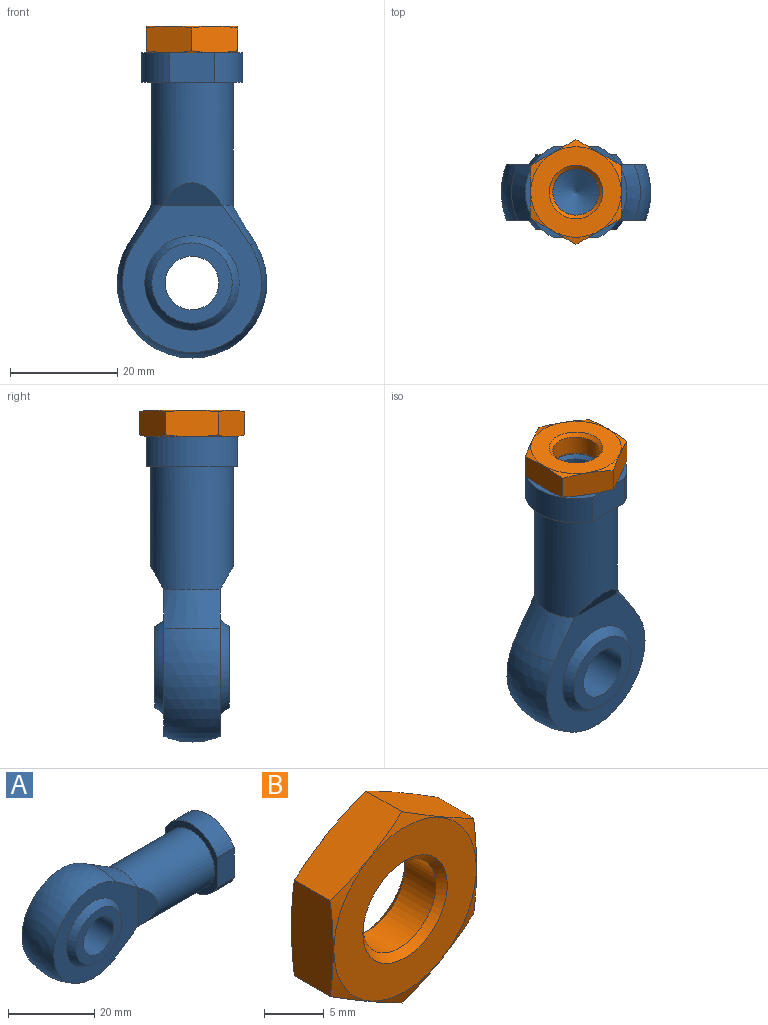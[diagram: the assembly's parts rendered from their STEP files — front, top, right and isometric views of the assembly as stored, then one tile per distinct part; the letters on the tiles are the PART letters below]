
ASSEMBLY  parts=2 mates=1
PART A: 22 faces, bbox 57x28x28 mm
  f0: cone r=866.03mm half-angle=60deg, axis (1,0,0), area 67.8mm2, adj f1
  f1: cylinder r=4.32mm len=24.32mm, axis (-1,0,0), area 660.8mm2, adj f0,f15
  f2: plane 8.49x5.55mm, normal (0,-1,0), area 47.1mm2, adj f3,f4,f9,f11
  f3: plane 19x17mm, normal (-1,0,0), area 87mm2, adj f2,f4,f5,f11,f20
  f4: cylinder r=9.5mm len=17mm, axis (-1,0,0), area 116.8mm2, adj f2,f3,f9,f20
  f5: cylinder r=7.68mm len=22.96mm, axis (-1,0,0), area 1037.9mm2, adj f3,f6,f8,f19,f21
  f6: cone r=12.04mm half-angle=30.7deg, axis (-1,0,0), area 94.9mm2, adj f5,f7,f10,f18
  f7: plane 27.47x25.96mm, normal (0,-1,0), area 318.1mm2, adj f6,f8,f10,f16,f21
  f8: plane 11.2x4.2mm, normal (-0.5,-0.87,0), area 37.6mm2, adj f5,f7
  f9: plane 19x17mm, normal (1,0,0), area 193.6mm2, adj f2,f4,f11,f15,f20
  f10: sphere r=14mm, area 623.8mm2, adj f6,f7,f18,f21
  f11: cylinder r=9.5mm len=17mm, axis (-1,0,0), area 116.8mm2, adj f2,f3,f9,f20
  f12: cylinder r=5mm len=14mm, axis (0,1,0), area 439.8mm2, adj f13,f17
  f13: plane 15x15mm, normal (0,-1,0), area 98.1mm2, adj f12,f16
  f14: sphere r=10.26mm, area 112.8mm2, adj f17,f18
  f15: cone r=4.32mm half-angle=45deg, axis (1,0,0), area 28mm2, adj f1,f9
  f16: sphere r=10.26mm, area 112.8mm2, adj f7,f13
  f17: plane 15x15mm, normal (0,1,0), area 98.1mm2, adj f12,f14
  f18: plane 27.47x25.96mm, normal (0,1,0), area 318.2mm2, adj f6,f10,f14,f19,f21
  f19: plane 11.2x4.2mm, normal (-0.5,0.87,0), area 37.6mm2, adj f5,f18
  f20: plane 8.49x5.55mm, normal (0,1,0), area 47.1mm2, adj f3,f4,f9,f11
  f21: cone r=12.04mm half-angle=30.7deg, axis (-1,0,0), area 94.9mm2, adj f5,f7,f10,f18
PART B: 13 faces, bbox 19.6x5x19.6 mm
  f0: plane 9.82x4.98mm, normal (-1,0,0), area 46.4mm2, adj f1,f2,f4,f8
  f1: plane 8.5x4.98mm, normal (-0.5,0,-0.87), area 46.4mm2, adj f0,f2,f8,f12
  f2: cone r=17.78mm half-angle=75deg, axis (0,1,0), area 26.9mm2, adj f0,f1,f3,f4,f5,f6,f12
  f3: plane 9.82x4.98mm, normal (1,0,0), area 46.4mm2, adj f2,f6,f8,f12
  f4: plane 8.5x4.98mm, normal (-0.5,0,0.87), area 46.4mm2, adj f0,f2,f6,f8
  f5: plane 16.9x16.9mm, normal (0,-1,0), area 145.8mm2, adj f2,f9
  f6: plane 8.5x4.98mm, normal (0.5,0,0.87), area 46.4mm2, adj f2,f3,f4,f8
  f7: plane 16.9x16.9mm, normal (0,1,0), area 145.8mm2, adj f8,f11
  f8: cone r=8.45mm half-angle=75deg, axis (0,-1,0), area 26.9mm2, adj f0,f1,f3,f4,f6,f7,f12
  f9: cone r=4.32mm half-angle=45deg, axis (0,-1,0), area 28mm2, adj f5,f10
  f10: cylinder r=4.32mm len=8.65mm, axis (0,1,0), area 99.1mm2, adj f9,f11
  f11: cone r=5mm half-angle=45deg, axis (0,1,0), area 28mm2, adj f7,f10
  f12: plane 8.5x4.98mm, normal (0.5,0,-0.87), area 46.4mm2, adj f1,f2,f3,f8
PLACE A rot(axis=(0,-1,0),90deg) t=(-2.97,-7.8,-25.56)mm
PLACE B rot(axis=(1,0,0),90deg) t=(-2.97,-7.8,22.44)mm
MATE fastened B.f2 <-> A.f0  axis (0,0,-1) through (-2.97,-7.8,17.44)mm
